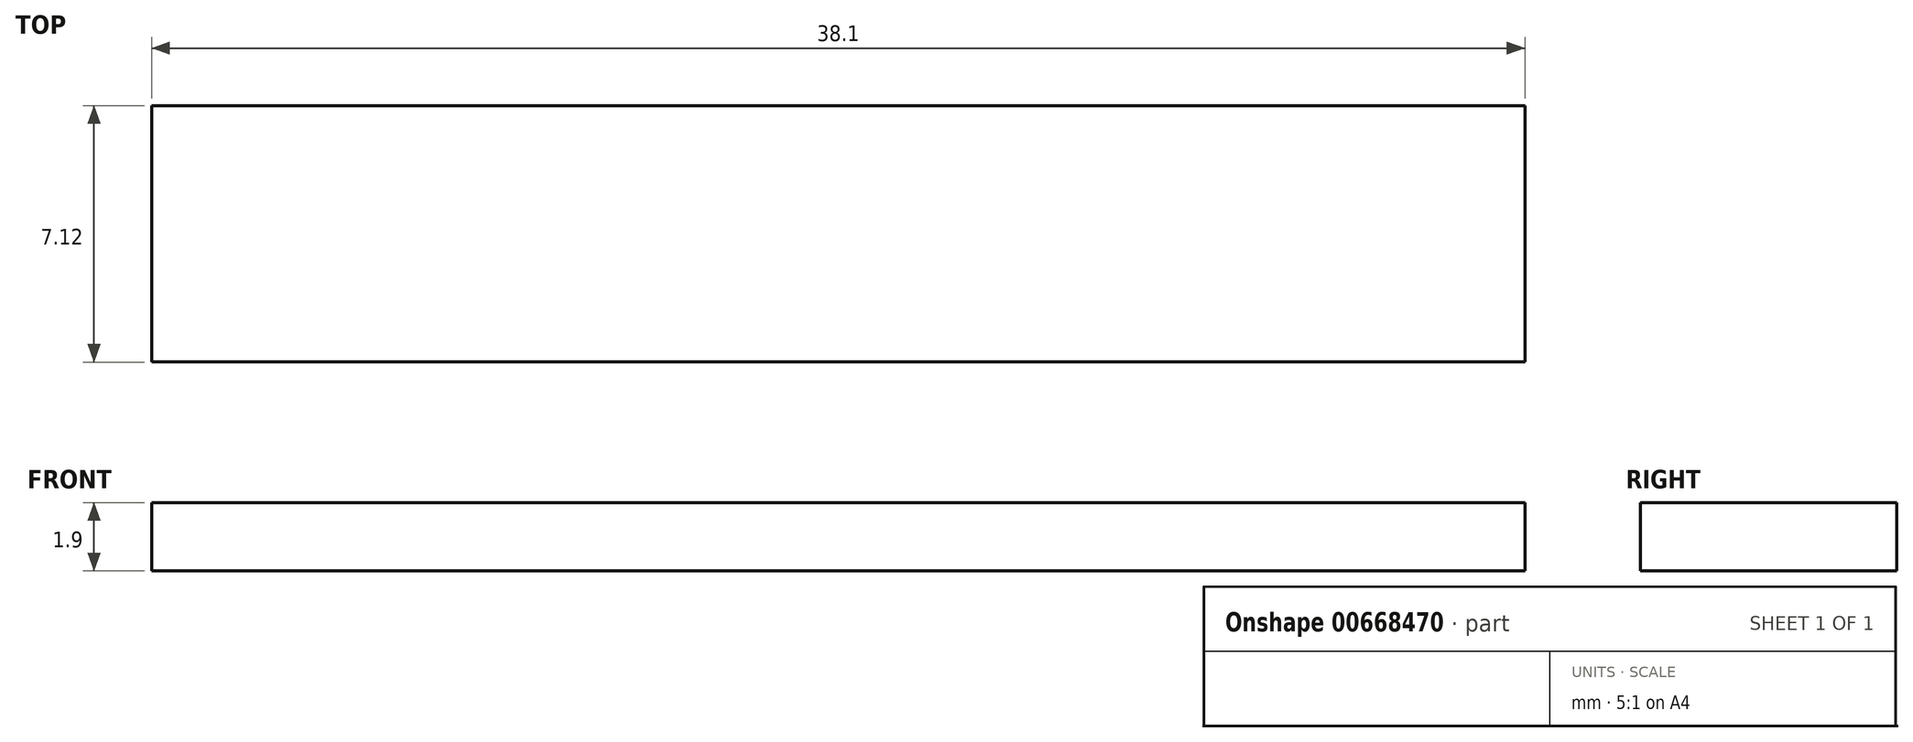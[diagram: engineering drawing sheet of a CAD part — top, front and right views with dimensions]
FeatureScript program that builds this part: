
annotation { "Feature Type Name" : "Feature", "Feature Type Description" : "" }
export const myFeature = defineFeature(function(context is Context, id is Id, definition is map)
    precondition{}
    {
        {
            var Q0;
            Q0=qCreatedBy(makeId("Top.planeOp"),FACE);
            var sketch = newSketch(context, id + "F0", { "sketchPlane" : qUnion([Q0])});
            skLineSegment(sketch, "E0.bottom", {"start": v(-16.65, 17.19) * mm, "end": v(21.45, 17.19) * mm});
            skLineSegment(sketch, "E0.top", {"start": v(-16.65, 10.07) * mm, "end": v(21.45, 10.07) * mm});
            skLineSegment(sketch, "E0.left", {"start": v(-16.65, 17.19) * mm, "end": v(-16.65, 10.07) * mm});
            skLineSegment(sketch, "E0.right", {"start": v(21.45, 17.19) * mm, "end": v(21.45, 10.07) * mm});
            skSolve(sketch);
        }
        {
            var Q0;
            Q0=makeQuery(id+"F0.imprint","IMPRINT",FACE,{"disambiguationData":[TD([[makeQuery(id+"F0.imprint","IMPRINT",EDGE,{"derivedFrom":sQuery(id+"F0.wireOp",EDGE,"E0.bottom")}),-1.0]])]});
            extrude(context, id + "F1", {"entities" : qUnion([Q0]), "depth" : 1.9 * mm});
        }
    });
